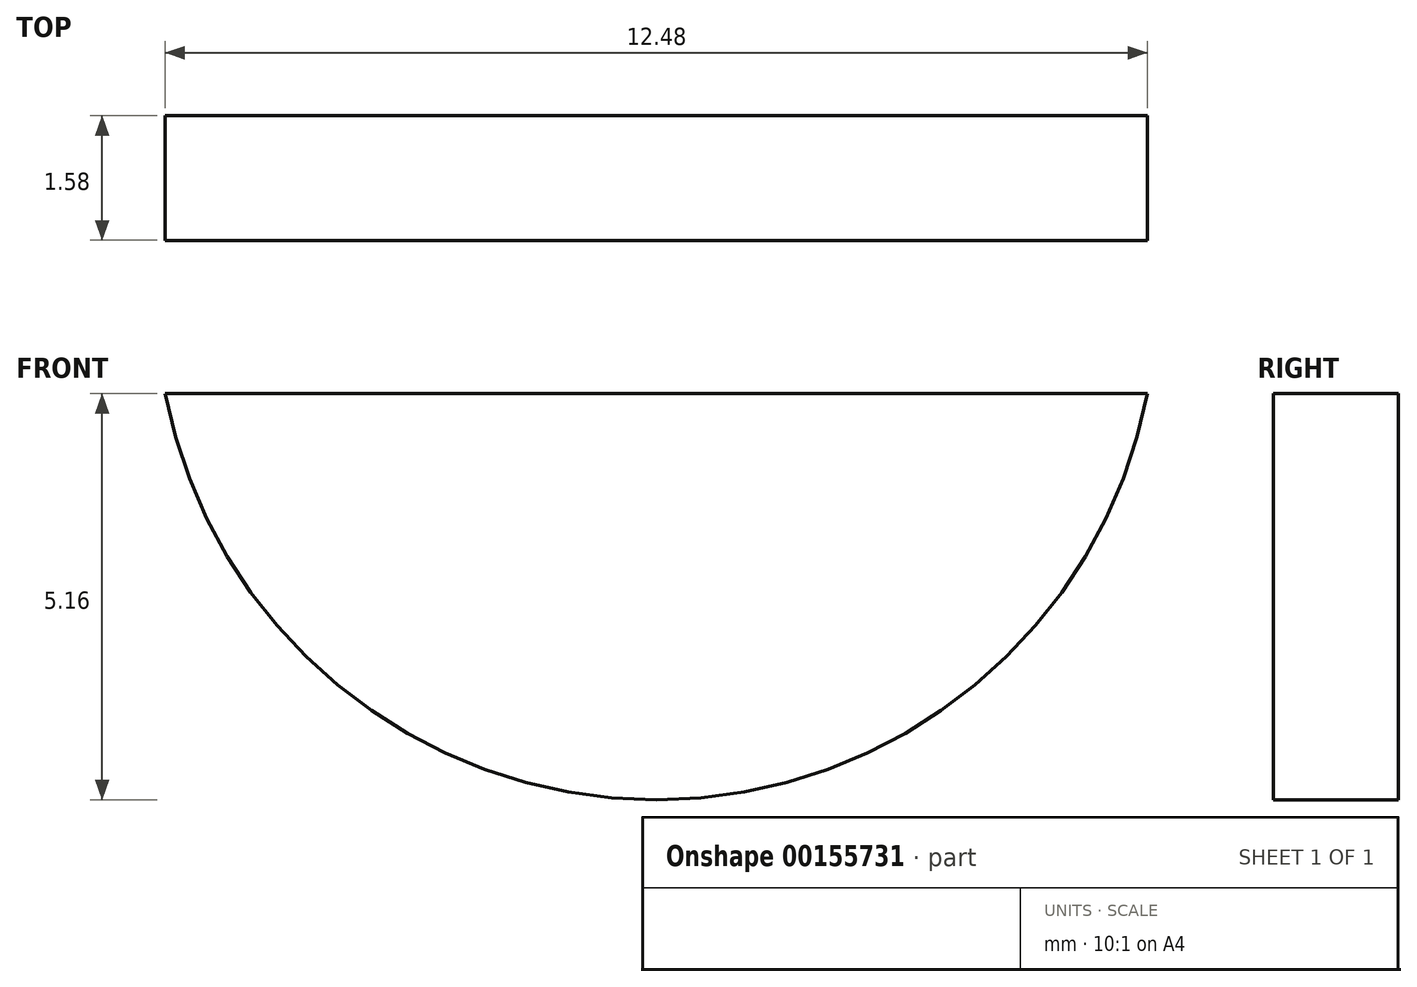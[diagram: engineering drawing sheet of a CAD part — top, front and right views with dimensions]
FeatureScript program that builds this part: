
annotation { "Feature Type Name" : "Feature", "Feature Type Description" : "" }
export const myFeature = defineFeature(function(context is Context, id is Id, definition is map)
    precondition{}
    {
        {
            var Q0;
            Q0=qCreatedBy(makeId("Front.planeOp"),FACE);
            var sketch = newSketch(context, id + "F0", { "sketchPlane" : qUnion([Q0])});
            skArc(sketch, "E0", {"start": v(-6.24, 0) * mm, "mid": v(0, -5.16) * mm, "end": v(6.24, 0) * mm});
            skLineSegment(sketch, "E1", {"start": v(-6.24, 0) * mm, "end": v(6.24, 0) * mm});
            skSolve(sketch);
        }
        {
            var Q0;
            Q0 = qSketchRegion(id + "F0", true);
            extrude(context, id + "F1", {"entities" : qUnion([Q0]), "endBound" : BoundingType.SYMMETRIC, "depth" : 1.59 * mm});
        }
    });
